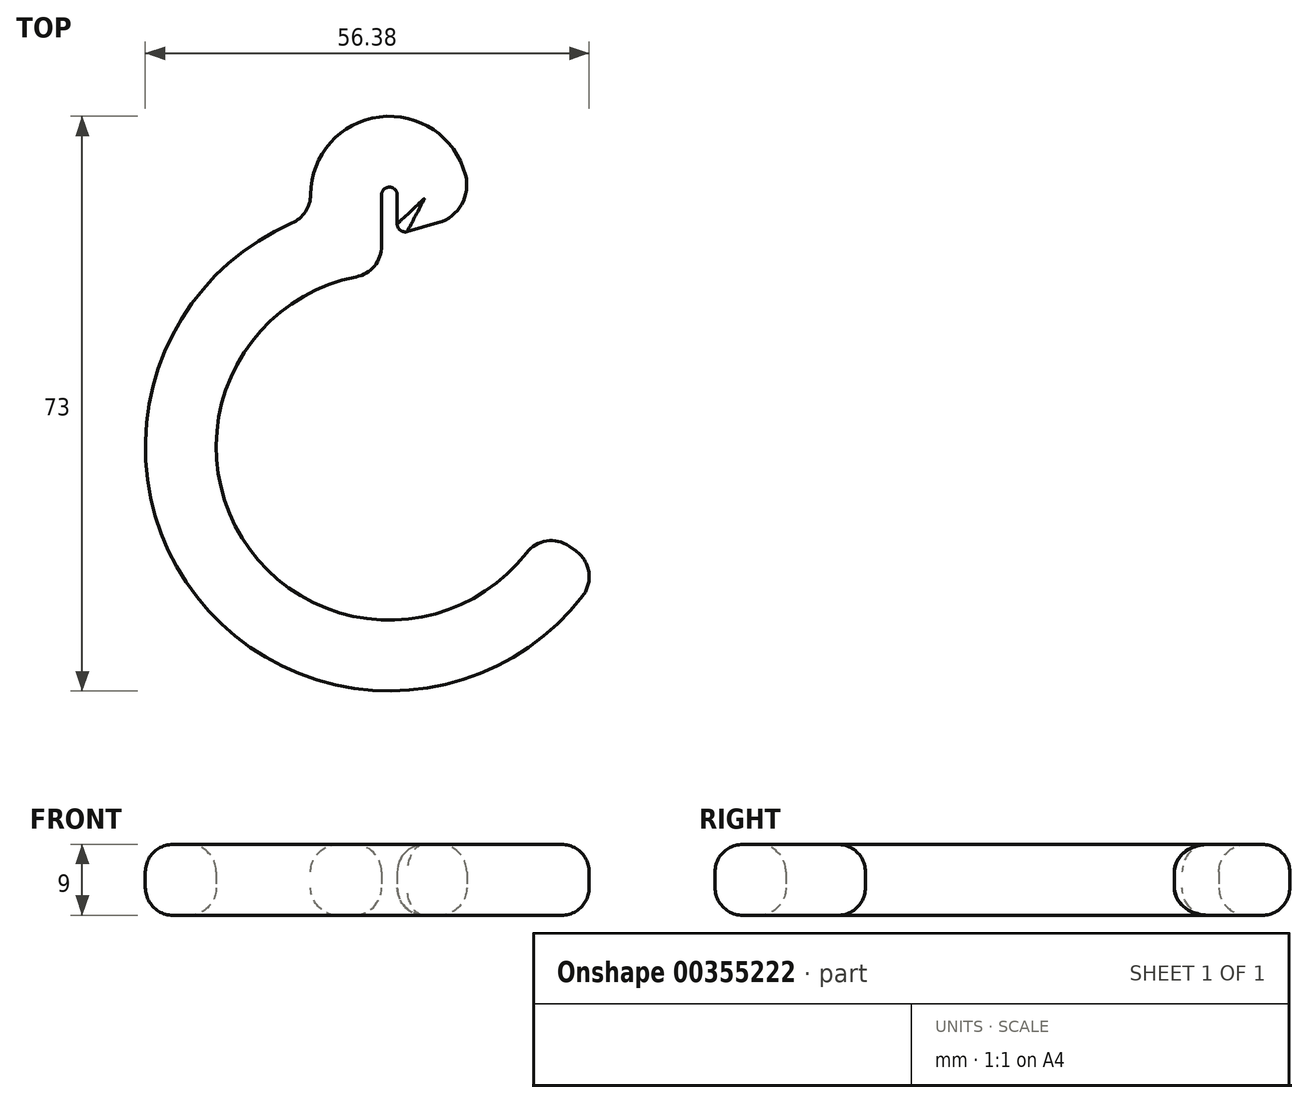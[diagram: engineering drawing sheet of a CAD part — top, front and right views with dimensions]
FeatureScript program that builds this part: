
annotation { "Feature Type Name" : "Feature", "Feature Type Description" : "" }
export const myFeature = defineFeature(function(context is Context, id is Id, definition is map)
    precondition{}
    {
        {
            var Q0;
            Q0=qCreatedBy(makeId("Top.planeOp"),FACE);
            var sketch = newSketch(context, id + "F0", { "sketchPlane" : qUnion([Q0])});
            skArc(sketch, "E0", {"start": v(1, 25.77) * mm, "mid": v(0, 26.77) * mm, "end": v(-1, 25.77) * mm});
            skLineSegment(sketch, "E1", {"start": v(0, 25.77) * mm, "end": v(0, -6.23) * mm});
            skArc(sketch, "E2", {"start": v(-4.23, 15.36) * mm, "mid": v(-18.72, -17.78) * mm, "end": v(17.4, -19.7) * mm});
            skArc(sketch, "E3.0", {"start": v(9.67, 28.32) * mm, "mid": v(-1.26, 35.7) * mm, "end": v(-10, 25.83) * mm});
            skArc(sketch, "E4.0", {"start": v(-12.4, 22.18) * mm, "mid": v(-24.44, -25.3) * mm, "end": v(24.55, -25.16) * mm});
            skLineSegment(sketch, "E5", {"start": v(-1, 25.77) * mm, "end": v(-1, 19.29) * mm});
            skLineSegment(sketch, "E6", {"start": v(1, 25.77) * mm, "end": v(1, 22.08) * mm});
            skLineSegment(sketch, "E7", {"start": v(22.86, -18.86) * mm, "end": v(23.68, -19.44) * mm});
            skLineSegment(sketch, "E8", {"start": v(6.2, 22.24) * mm, "end": v(2.27, 21.12) * mm});
            skPoint(sketch, "E9.orphan", {"position": v(1, 15.75) * mm});
            skArc(sketch, "E10.filletArc", {"start": v(22.86, -18.86) * mm, "mid": v(19.96, -18.19) * mm, "end": v(17.4, -19.7) * mm});
            skPoint(sketch, "E11.visualSharp", {"position": v(26.88, -21.68) * mm});
            skArc(sketch, "E11.filletArc", {"start": v(24.55, -25.16) * mm, "mid": v(25.34, -22.11) * mm, "end": v(23.68, -19.44) * mm});
            skPoint(sketch, "E12.visualSharp", {"position": v(-1, 15.75) * mm});
            skArc(sketch, "E12.filletArc", {"start": v(-4.23, 15.36) * mm, "mid": v(-1.91, 16.74) * mm, "end": v(-1, 19.29) * mm});
            skPoint(sketch, "E13.visualSharp", {"position": v(-9.67, 23.22) * mm});
            skArc(sketch, "E13.filletArc", {"start": v(-12.4, 22.18) * mm, "mid": v(-10.66, 23.65) * mm, "end": v(-10, 25.83) * mm});
            skPoint(sketch, "E14.visualSharp", {"position": v(1, 20.76) * mm});
            skArc(sketch, "E14.filletArc", {"start": v(1, 22.08) * mm, "mid": v(1.4, 21.29) * mm, "end": v(2.27, 21.12) * mm});
            skPoint(sketch, "E15.visualSharp", {"position": v(9.67, 23.22) * mm});
            skArc(sketch, "E15.filletArc", {"start": v(6.2, 22.24) * mm, "mid": v(9.18, 24.57) * mm, "end": v(9.67, 28.32) * mm});
            skSolve(sketch);
        }
        {
            var Q0;
            Q0=makeQuery(id+"F0.imprint","IMPRINT",FACE,{"disambiguationData":[TD([[makeQuery(id+"F0.imprint","IMPRINT",EDGE,{"derivedFrom":sQuery(id+"F0.wireOp",EDGE,"E0")}),-1.0]])]});
            extrude(context, id + "F1", {"entities" : qUnion([Q0]), "depth" : 9 * mm});
        }
        {
            var Q0;
            Q0=makeQuery(id+"F1.opExtrude","CAP_FACE",FACE,{"disambiguationData":[OSD([sQuery(id+"F0.wireOp",EDGE,"E0"),sQuery(id+"F0.wireOp",EDGE,"E2"),sQuery(id+"F0.wireOp",EDGE,"E3.0"),sQuery(id+"F0.wireOp",EDGE,"E4.0"),sQuery(id+"F0.wireOp",EDGE,"E5"),sQuery(id+"F0.wireOp",EDGE,"E6"),sQuery(id+"F0.wireOp",EDGE,"E7"),sQuery(id+"F0.wireOp",EDGE,"E8"),sQuery(id+"F0.wireOp",EDGE,"E10.filletArc"),sQuery(id+"F0.wireOp",EDGE,"E11.filletArc"),sQuery(id+"F0.wireOp",EDGE,"E12.filletArc"),sQuery(id+"F0.wireOp",EDGE,"E13.filletArc"),sQuery(id+"F0.wireOp",EDGE,"E14.filletArc"),sQuery(id+"F0.wireOp",EDGE,"E15.filletArc")])],"isStart":false});
            var Q1;
            Q1=makeQuery(id+"F1.opExtrude","CAP_FACE",FACE,{"disambiguationData":[OSD([sQuery(id+"F0.wireOp",EDGE,"E0"),sQuery(id+"F0.wireOp",EDGE,"E2"),sQuery(id+"F0.wireOp",EDGE,"E3.0"),sQuery(id+"F0.wireOp",EDGE,"E4.0"),sQuery(id+"F0.wireOp",EDGE,"E5"),sQuery(id+"F0.wireOp",EDGE,"E6"),sQuery(id+"F0.wireOp",EDGE,"E7"),sQuery(id+"F0.wireOp",EDGE,"E8"),sQuery(id+"F0.wireOp",EDGE,"E10.filletArc"),sQuery(id+"F0.wireOp",EDGE,"E11.filletArc"),sQuery(id+"F0.wireOp",EDGE,"E12.filletArc"),sQuery(id+"F0.wireOp",EDGE,"E13.filletArc"),sQuery(id+"F0.wireOp",EDGE,"E14.filletArc"),sQuery(id+"F0.wireOp",EDGE,"E15.filletArc")])],"isStart":true});
            fillet(context, id + "F2", {"entities" : qUnion([Q0, Q1]), "radius" : 3.5 * mm, "tangentPropagation" : true, "allowEdgeOverflow" : false});
        }
    });
